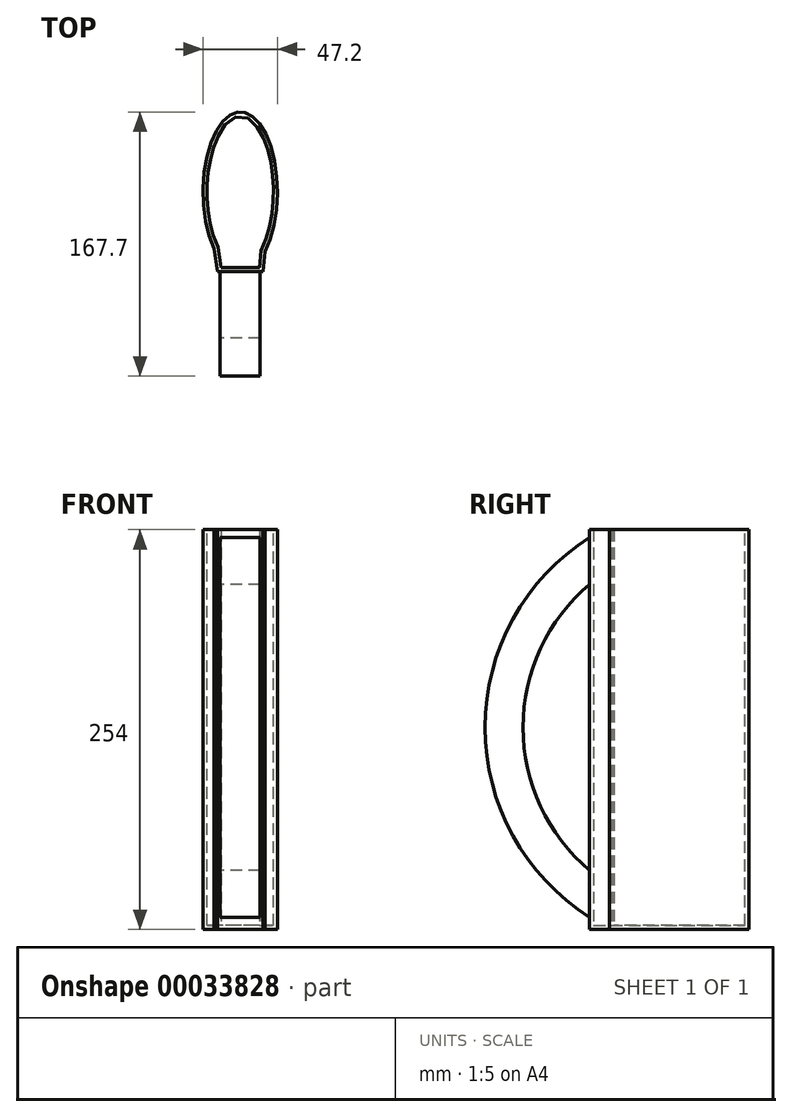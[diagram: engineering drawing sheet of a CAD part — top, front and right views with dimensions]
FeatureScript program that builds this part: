
annotation { "Feature Type Name" : "Feature", "Feature Type Description" : "" }
export const myFeature = defineFeature(function(context is Context, id is Id, definition is map)
    precondition{}
    {
        {
            var Q0;
            Q0=qCreatedBy(makeId("Top.planeOp"),FACE);
            var sketch = newSketch(context, id + "F0", { "sketchPlane" : qUnion([Q0])});
            skEllipticalArc(sketch, "E0", {});
            skLineSegment(sketch, "E1", {"start": v(0, -50.64) * mm, "end": v(14.51, -50.64) * mm});
            skLineSegment(sketch, "E2", {"start": v(14.51, -50.64) * mm, "end": v(0, -50.64) * mm});
            skLineSegment(sketch, "E3", {"start": v(0, -50.64) * mm, "end": v(-14.51, -50.64) * mm});
            skLineSegment(sketch, "E4", {"start": v(-14.51, -50.64) * mm, "end": v(-16.63, -35.94) * mm});
            skLineSegment(sketch, "E5", {"start": v(14.51, -50.64) * mm, "end": v(15.6, -38) * mm});
            const initialGuessF0  = {"E0": [0, 0, 0, -1, 0.0506363112086142, 0.02360360346050814, 0.7218762834391894, 5.501661850803666]};
            skSetInitialGuess(sketch, initialGuessF0);
            skSolve(sketch);
        }
        {
            var Q0;
            Q0=makeQuery(id+"F0.imprint","IMPRINT",FACE,{"disambiguationData":[TD([[makeQuery(id+"F0.imprint","IMPRINT",EDGE,{"derivedFrom":sQuery(id+"F0.wireOp",EDGE,"E0")}),1.0]])]});
            extrude(context, id + "F1", {"entities" : qUnion([Q0]), "depth" : 254 * mm});
        }
        {
            var Q0;
            Q0=qCreatedBy(makeId("Right.planeOp"),FACE);
            var sketch = newSketch(context, id + "F2", { "sketchPlane" : qUnion([Q0])});
            skLineSegment(sketch, "E6", {"start": v(-50.64, 0) * mm, "end": v(-50.64, 254) * mm});
            skArc(sketch, "E7", {"start": v(-50.64, 249.03) * mm, "mid": v(-117.06, 128.36) * mm, "end": v(-50.64, 7.7) * mm});
            skArc(sketch, "E8.0", {"start": v(-50.64, 219.23) * mm, "mid": v(-92.95, 128.36) * mm, "end": v(-50.64, 37.5) * mm});
            skPoint(sketch, "E9", {"position": v(-50.64, 219.23) * mm});
            skPoint(sketch, "E10", {"position": v(-50.64, 37.5) * mm});
            skSolve(sketch);
        }
        {
            var Q0;
            {var subQ1=sQuery(id+"F2.wireOp",EDGE,"E7");Q0=makeQuery(id+"F2.imprint","IMPRINT",FACE,{"disambiguationData":[TD([[makeQuery(id+"F2.imprint","IMPRINT",EDGE,{"derivedFrom":subQ1}),1.0]])]});}
            extrude(context, id + "F3", {"entities" : qUnion([Q0]), "endBound" : BoundingType.SYMMETRIC, "depth" : 25.4 * mm});
        }
        {
            var Q0;
            Q0=makeQuery(id+"F1.opExtrude","CAP_FACE",FACE,{"disambiguationData":[OSD([sQuery(id+"F0.wireOp",EDGE,"E0")])],"isStart":false});
            shell(context, id + "F4", {"entities" : qUnion([Q0]), "thickness" : 2.54 * mm});
        }
    });
